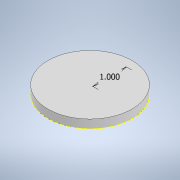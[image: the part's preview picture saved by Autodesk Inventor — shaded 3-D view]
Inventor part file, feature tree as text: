
AUTODESK INVENTOR PART (.ipt)
format: ipt  version: 2020 (Build 240168000, 168)  size: 184,832 bytes
history: native  units: in
note: dims shown in document units (in); Inventor stores cm internally (conversion verified against a paired STEP export)
features: sketch x3, extrude x1, emboss x1
ambient origin geometry x8: Origin, YZ Plane, XZ Plane, XY Plane, X Axis, Y Axis, Z Axis, Center Point
bodies: Solid1 (feature_tree)
feature tree (5):
  extrude  "Extrusion1"  Depth=0.25in TaperAngle=0.0deg
  emboss  "Emboss1"
  sketch  "Sketch3"  dims[d5=1.0in]
  sketch  "Sketch1"  dims[d0=2.5in d1=0.25in d2=0.0in]
  sketch  "Sketch2"  dims[d3=0.02in d4=0.0in]
